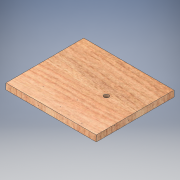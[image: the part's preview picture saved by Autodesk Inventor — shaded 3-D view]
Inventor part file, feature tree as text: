
AUTODESK INVENTOR PART (.ipt)
format: ipt  version: 2017 (Build 210142000, 142)  size: 126,976 bytes
history: native  units: in
note: dims shown in document units (in); Inventor stores cm internally (conversion verified against a paired STEP export)
features: extrude x2, sketch x2, projected_geometry x1
ambient origin geometry x8: Origin, YZ Plane, XZ Plane, XY Plane, X Axis, Y Axis, Z Axis, Center Point
bodies: Solid1 (feature_tree)
feature tree (5):
  extrude  "Extrusion1"  Depth=6.0in
  extrude  "Extrusion2"  Depth=0.4688in
  sketch  "Sketch1"  dims[d0=6.9688in d1=6.0in]
  sketch  "Sketch2"  dims[d2=0.4688in d3=0.0in d4=2.2188in d5=0.375in d6=0.4688in d7=0.0in]
  projected_geometry  "Projected Loop1"
